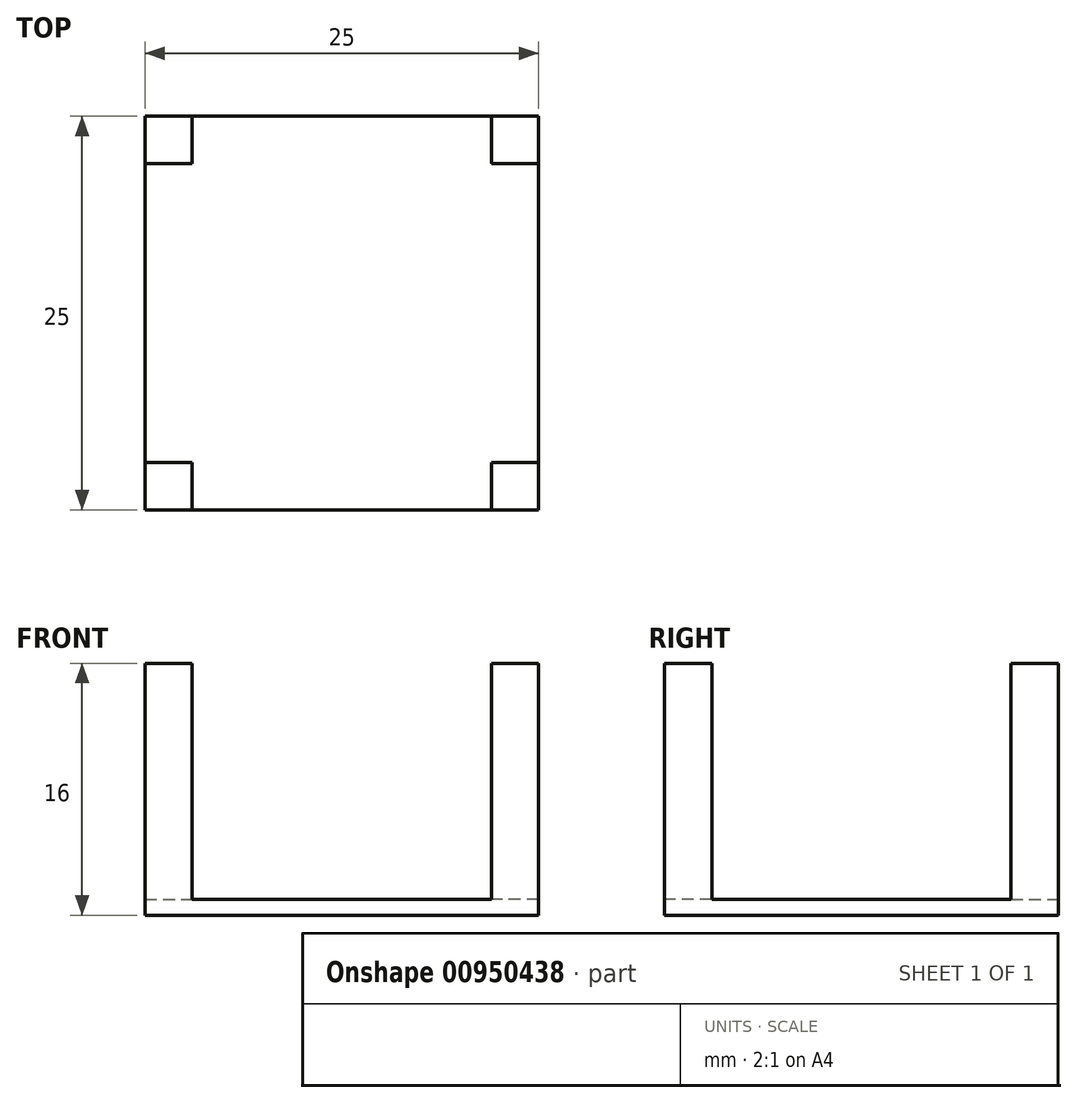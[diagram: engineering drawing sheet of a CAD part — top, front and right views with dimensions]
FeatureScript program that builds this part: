
annotation { "Feature Type Name" : "Feature", "Feature Type Description" : "" }
export const myFeature = defineFeature(function(context is Context, id is Id, definition is map)
    precondition{}
    {
        {
            var Q0;
            Q0=qCreatedBy(makeId("Top.planeOp"),FACE);
            var sketch = newSketch(context, id + "F0", { "sketchPlane" : qUnion([Q0])});
            skLineSegment(sketch, "E0.bottom", {"start": v(-12.5, 12.5) * mm, "end": v(12.5, 12.5) * mm});
            skLineSegment(sketch, "E0.top", {"start": v(-12.5, -12.5) * mm, "end": v(12.5, -12.5) * mm});
            skLineSegment(sketch, "E0.left", {"start": v(-12.5, 12.5) * mm, "end": v(-12.5, -12.5) * mm});
            skLineSegment(sketch, "E0.right", {"start": v(12.5, 12.5) * mm, "end": v(12.5, -12.5) * mm});
            skSolve(sketch);
        }
        {
            var Q0;
            Q0 = qSketchRegion(id + "F0", true);
            extrude(context, id + "F1", {"entities" : qUnion([Q0]), "depth" : 1 * mm, "offsetDistance" : 25 * mm});
        }
        {
            var Q0;
            Q0=makeQuery(id+"F1.opExtrude","CAP_FACE",FACE,{"disambiguationData":[OSD([sQuery(id+"F0.wireOp",EDGE,"E0.bottom"),sQuery(id+"F0.wireOp",EDGE,"E0.top"),sQuery(id+"F0.wireOp",EDGE,"E0.left"),sQuery(id+"F0.wireOp",EDGE,"E0.right")])],"isStart":false});
            var sketch = newSketch(context, id + "F2", { "sketchPlane" : qUnion([Q0])});
            skLineSegment(sketch, "E1.bottom", {"start": v(-12.5, 9.5) * mm, "end": v(-9.5, 9.5) * mm});
            skLineSegment(sketch, "E1.top", {"start": v(-12.5, 12.5) * mm, "end": v(-9.5, 12.5) * mm});
            skLineSegment(sketch, "E1.left", {"start": v(-12.5, 9.5) * mm, "end": v(-12.5, 12.5) * mm});
            skLineSegment(sketch, "E1.right", {"start": v(-9.5, 9.5) * mm, "end": v(-9.5, 12.5) * mm});
            skPoint(sketch, "E2.oppositeSnap0", {"position": v(0, -12.5) * mm});
            skLineSegment(sketch, "E2.bottom", {"start": v(-12.5, -9.5) * mm, "end": v(-9.5, -9.5) * mm});
            skLineSegment(sketch, "E2.top", {"start": v(-12.5, -12.5) * mm, "end": v(-9.5, -12.5) * mm});
            skLineSegment(sketch, "E2.left", {"start": v(-12.5, -9.5) * mm, "end": v(-12.5, -12.5) * mm});
            skLineSegment(sketch, "E2.right", {"start": v(-9.5, -9.5) * mm, "end": v(-9.5, -12.5) * mm});
            skLineSegment(sketch, "E3.bottom", {"start": v(9.5, -12.5) * mm, "end": v(12.5, -12.5) * mm});
            skLineSegment(sketch, "E3.top", {"start": v(9.5, -9.5) * mm, "end": v(12.5, -9.5) * mm});
            skLineSegment(sketch, "E3.left", {"start": v(9.5, -12.5) * mm, "end": v(9.5, -9.5) * mm});
            skLineSegment(sketch, "E3.right", {"start": v(12.5, -12.5) * mm, "end": v(12.5, -9.5) * mm});
            skLineSegment(sketch, "E4.bottom", {"start": v(12.5, 9.5) * mm, "end": v(9.5, 9.5) * mm});
            skLineSegment(sketch, "E4.top", {"start": v(12.5, 12.5) * mm, "end": v(9.5, 12.5) * mm});
            skLineSegment(sketch, "E4.left", {"start": v(12.5, 9.5) * mm, "end": v(12.5, 12.5) * mm});
            skLineSegment(sketch, "E4.right", {"start": v(9.5, 9.5) * mm, "end": v(9.5, 12.5) * mm});
            skSolve(sketch);
        }
        {
            var Q0;
            Q0=makeQuery(id+"F2.imprint","IMPRINT",FACE,{"disambiguationData":[TD([[makeQuery(id+"F2.imprint","IMPRINT",EDGE,{"derivedFrom":sQuery(id+"F2.wireOp",EDGE,"E1.bottom")}),1.0]])]});
            var Q1;
            Q1=makeQuery(id+"F2.imprint","IMPRINT",FACE,{"disambiguationData":[TD([[makeQuery(id+"F2.imprint","IMPRINT",EDGE,{"derivedFrom":sQuery(id+"F2.wireOp",EDGE,"E4.bottom")}),-1.0]])]});
            var Q2;
            Q2=makeQuery(id+"F2.imprint","IMPRINT",FACE,{"disambiguationData":[TD([[makeQuery(id+"F2.imprint","IMPRINT",EDGE,{"derivedFrom":sQuery(id+"F2.wireOp",EDGE,"E3.bottom")}),1.0]])]});
            var Q3;
            Q3=makeQuery(id+"F2.imprint","IMPRINT",FACE,{"disambiguationData":[TD([[makeQuery(id+"F2.imprint","IMPRINT",EDGE,{"derivedFrom":sQuery(id+"F2.wireOp",EDGE,"E2.bottom")}),-1.0]])]});
            extrude(context, id + "F3", {"entities" : qUnion([Q0, Q1, Q2, Q3]), "operationType" : NewBodyOperationType.ADD, "depth" : 15 * mm, "offsetDistance" : 25 * mm});
        }
    });
